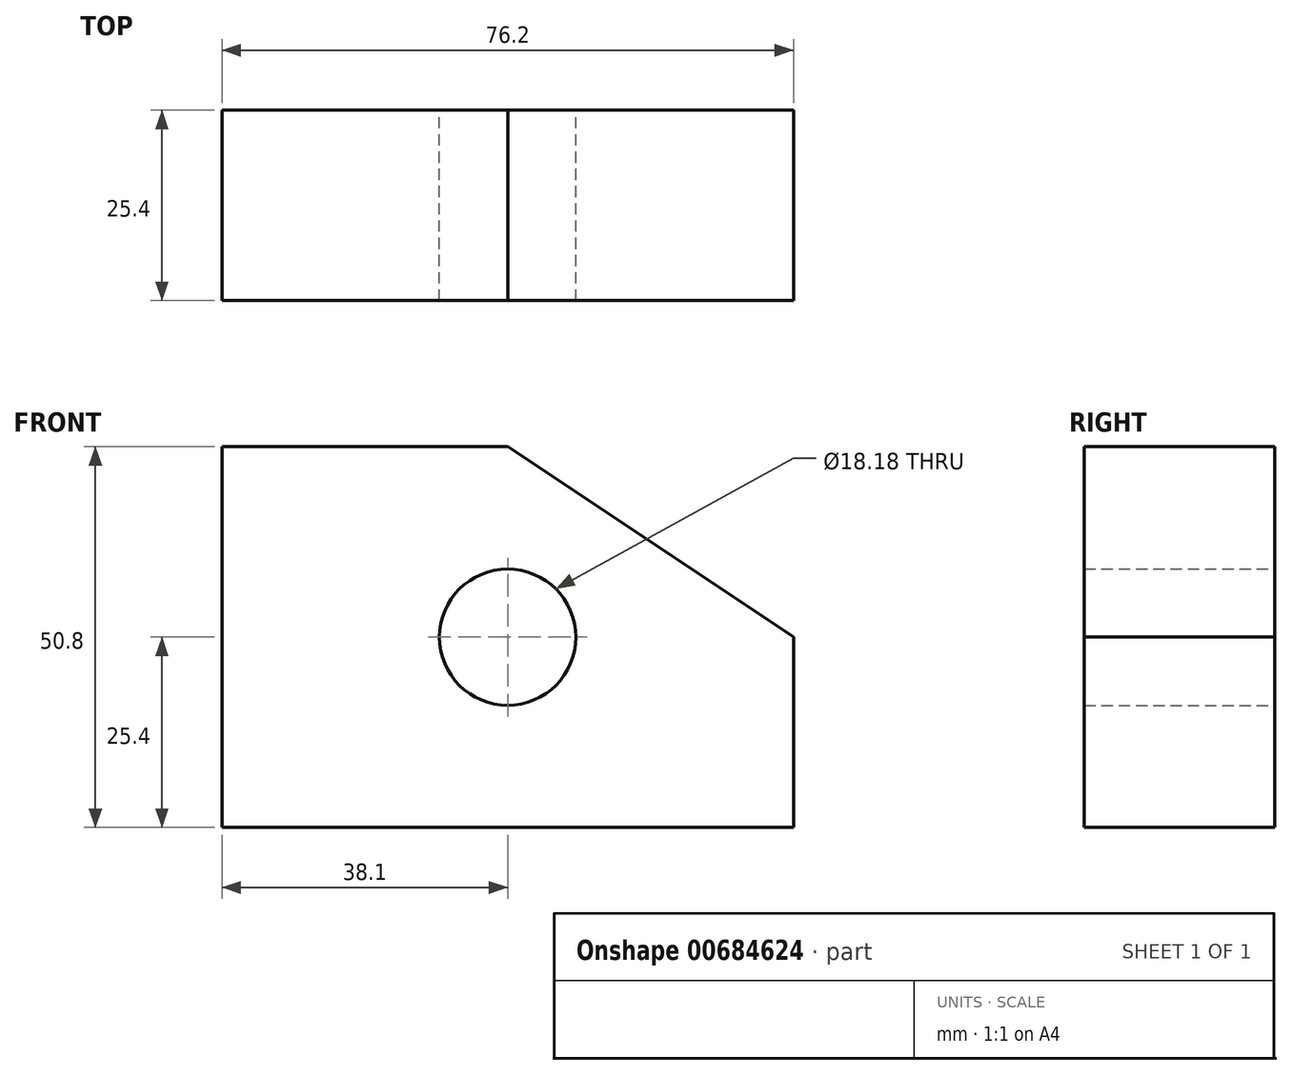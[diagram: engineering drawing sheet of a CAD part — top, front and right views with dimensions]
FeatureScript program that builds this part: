
annotation { "Feature Type Name" : "Feature", "Feature Type Description" : "" }
export const myFeature = defineFeature(function(context is Context, id is Id, definition is map)
    precondition{}
    {
        {
            var Q0;
            Q0=qCreatedBy(makeId("Front.planeOp"),FACE);
            var sketch = newSketch(context, id + "F0", { "sketchPlane" : qUnion([Q0])});
            skLineSegment(sketch, "E0", {"start": v(-38.1, 25.4) * mm, "end": v(-38.1, -25.4) * mm});
            skLineSegment(sketch, "E1", {"start": v(-38.1, 25.4) * mm, "end": v(0, 25.4) * mm});
            skLineSegment(sketch, "E2", {"start": v(-38.1, -25.4) * mm, "end": v(38.1, -25.4) * mm});
            skLineSegment(sketch, "E3", {"start": v(38.1, -25.4) * mm, "end": v(38.1, 0) * mm});
            skLineSegment(sketch, "E4", {"start": v(38.1, 0) * mm, "end": v(0, 25.4) * mm});
            skCircle(sketch, "E5", {"center": v(0, 0) * mm, "radius": 9.1 * mm});
            skSolve(sketch);
        }
        {
            var Q0;
            Q0=makeQuery(id+"F0.imprint","IMPRINT",FACE,{"disambiguationData":[TD([[makeQuery(id+"F0.imprint","IMPRINT",EDGE,{"derivedFrom":sQuery(id+"F0.wireOp",EDGE,"E0")}),1.0]])]});
            extrude(context, id + "F1", {"entities" : qUnion([Q0]), "depth" : 25.4 * mm, "offsetDistance" : 25.4 * mm});
        }
    });
